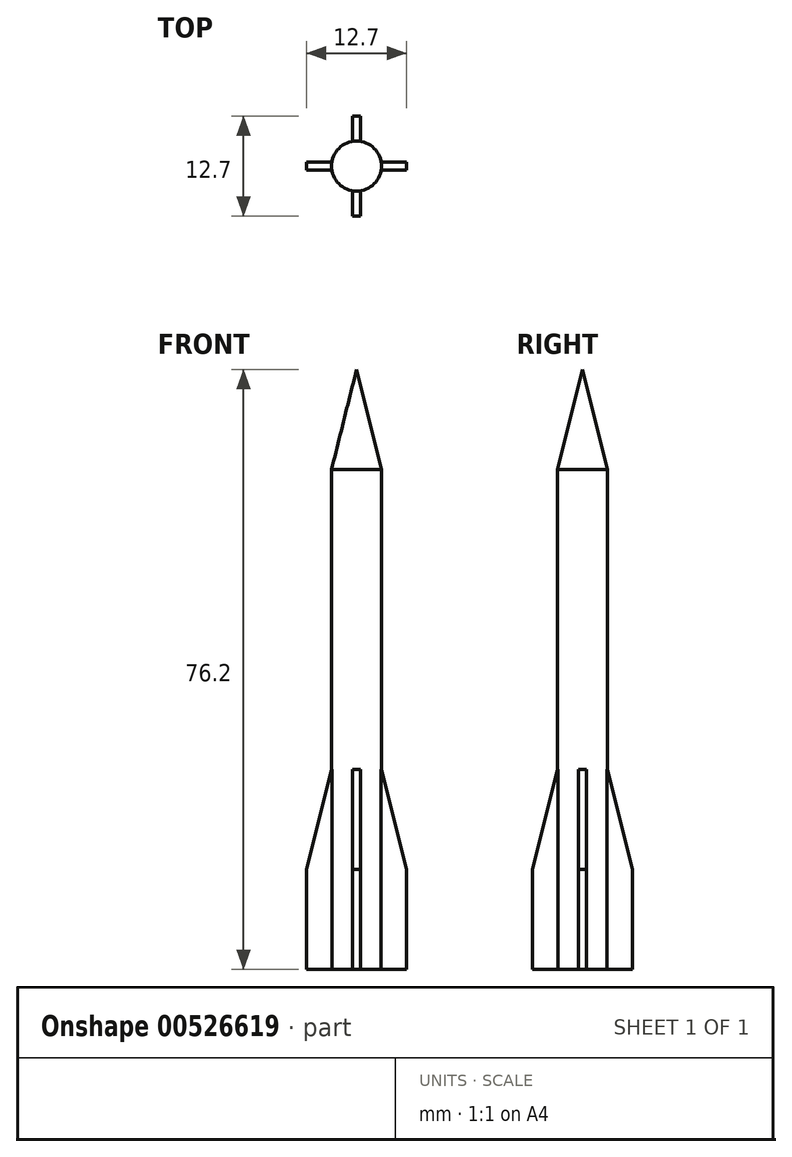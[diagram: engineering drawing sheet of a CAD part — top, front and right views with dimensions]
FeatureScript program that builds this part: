
annotation { "Feature Type Name" : "Feature", "Feature Type Description" : "" }
export const myFeature = defineFeature(function(context is Context, id is Id, definition is map)
    precondition{}
    {
        {
            var Q0;
            Q0=qCreatedBy(makeId("Top.planeOp"),FACE);
            var sketch = newSketch(context, id + "F0", { "sketchPlane" : qUnion([Q0])});
            skCircle(sketch, "E0", {"center": v(0, 0) * mm, "radius": 3.18 * mm});
            skLineSegment(sketch, "E1.bottom", {"start": v(6.35, 0.5) * mm, "end": v(-6.35, 0.5) * mm});
            skLineSegment(sketch, "E1.top", {"start": v(6.35, -0.5) * mm, "end": v(-6.35, -0.5) * mm});
            skLineSegment(sketch, "E1.left", {"start": v(6.35, 0.5) * mm, "end": v(6.35, -0.5) * mm});
            skLineSegment(sketch, "E1.right", {"start": v(-6.35, 0.5) * mm, "end": v(-6.35, -0.5) * mm});
            skLineSegment(sketch, "E2.bottom", {"start": v(0.5, 6.35) * mm, "end": v(-0.5, 6.35) * mm});
            skLineSegment(sketch, "E2.top", {"start": v(0.5, -6.35) * mm, "end": v(-0.5, -6.35) * mm});
            skLineSegment(sketch, "E2.left", {"start": v(0.5, 6.35) * mm, "end": v(0.5, -6.35) * mm});
            skLineSegment(sketch, "E2.right", {"start": v(-0.5, 6.35) * mm, "end": v(-0.5, -6.35) * mm});
            skSolve(sketch);
        }
        {
            var Q0;
            Q0=qCreatedBy(makeId("Front.planeOp"),FACE);
            var sketch = newSketch(context, id + "F1", { "sketchPlane" : qUnion([Q0])});
            skLineSegment(sketch, "E3", {"start": v(0, 0) * mm, "end": v(0, 76.2) * mm});
            skLineSegment(sketch, "E4", {"start": v(0, 0) * mm, "end": v(6.42, 0) * mm});
            skLineSegment(sketch, "E5", {"start": v(0, 0) * mm, "end": v(3.18, 0) * mm});
            skLineSegment(sketch, "E6", {"start": v(3.18, 0) * mm, "end": v(3.18, 63.5) * mm});
            skLineSegment(sketch, "E7", {"start": v(3.17, 63.5) * mm, "end": v(0, 76.2) * mm});
            skSolve(sketch);
        }
        {
            var Q0;
            Q0=makeQuery(id+"F1.imprint","IMPRINT",FACE,{"disambiguationData":[TD([[makeQuery(id+"F1.imprint","IMPRINT",EDGE,{"derivedFrom":sQuery(id+"F1.wireOp",EDGE,"E3")}),-1.0]])]});
            var Q1;
            Q1=sQuery(id+"F1.wireOp",EDGE,"E3");
            revolve(context, id + "F2", {"entities" : qUnion([Q0]), "axis" : qUnion([Q1]), "revolveType" : RevolveType.FULL});
        }
        {
            var Q0;
            {var subQ5=sQuery(id+"F0.wireOp",EDGE,"E1.left");Q0=makeQuery(id+"F0.imprint","IMPRINT",FACE,{"disambiguationData":[TD([[makeQuery(id+"F0.imprint","IMPRINT",EDGE,{"derivedFrom":subQ5}),-1.0]])]});}
            var Q1;
            {var subQ5=sQuery(id+"F0.wireOp",EDGE,"E2.top");Q1=makeQuery(id+"F0.imprint","IMPRINT",FACE,{"disambiguationData":[TD([[makeQuery(id+"F0.imprint","IMPRINT",EDGE,{"derivedFrom":subQ5}),-1.0]])]});}
            var Q2;
            {var subQ5=sQuery(id+"F0.wireOp",EDGE,"E1.right");Q2=makeQuery(id+"F0.imprint","IMPRINT",FACE,{"disambiguationData":[TD([[makeQuery(id+"F0.imprint","IMPRINT",EDGE,{"derivedFrom":subQ5}),1.0]])]});}
            var Q3;
            {var subQ5=sQuery(id+"F0.wireOp",EDGE,"E2.bottom");Q3=makeQuery(id+"F0.imprint","IMPRINT",FACE,{"disambiguationData":[TD([[makeQuery(id+"F0.imprint","IMPRINT",EDGE,{"derivedFrom":subQ5}),1.0]])]});}
            extrude(context, id + "F3", {"entities" : qUnion([Q0, Q1, Q2, Q3]), "operationType" : NewBodyOperationType.ADD, "depth" : 25.4 * mm, "offsetDistance" : 25.4 * mm});
        }
        {
            var Q0;
            Q0=makeQuery(id+"F3.opExtrude","CAP_EDGE",EDGE,{"disambiguationData":[OSD([sQuery(id+"F0.wireOp",EDGE,"E2.top")])],"isStart":false});
            var Q1;
            Q1=makeQuery(id+"F3.opExtrude","CAP_EDGE",EDGE,{"disambiguationData":[OSD([sQuery(id+"F0.wireOp",EDGE,"E1.left")])],"isStart":false});
            chamfer(context, id + "F4", {"entities" : qUnion([Q0, Q1]), "chamferType" : ChamferType.TWO_OFFSETS, "width1" : 3.17 * mm, "oppositeDirection" : true, "width2" : 12.7 * mm, "tangentPropagation" : true});
        }
        {
            var Q0;
            Q0=makeQuery(id+"F3.opExtrude","CAP_EDGE",EDGE,{"disambiguationData":[OSD([sQuery(id+"F0.wireOp",EDGE,"E1.right")])],"isStart":false});
            var Q1;
            Q1=makeQuery(id+"F3.opExtrude","CAP_EDGE",EDGE,{"disambiguationData":[OSD([sQuery(id+"F0.wireOp",EDGE,"E2.bottom")])],"isStart":false});
            chamfer(context, id + "F5", {"entities" : qUnion([Q0, Q1]), "chamferType" : ChamferType.TWO_OFFSETS, "width1" : 3.17 * mm, "oppositeDirection" : false, "width2" : 12.7 * mm, "tangentPropagation" : true});
        }
    });
